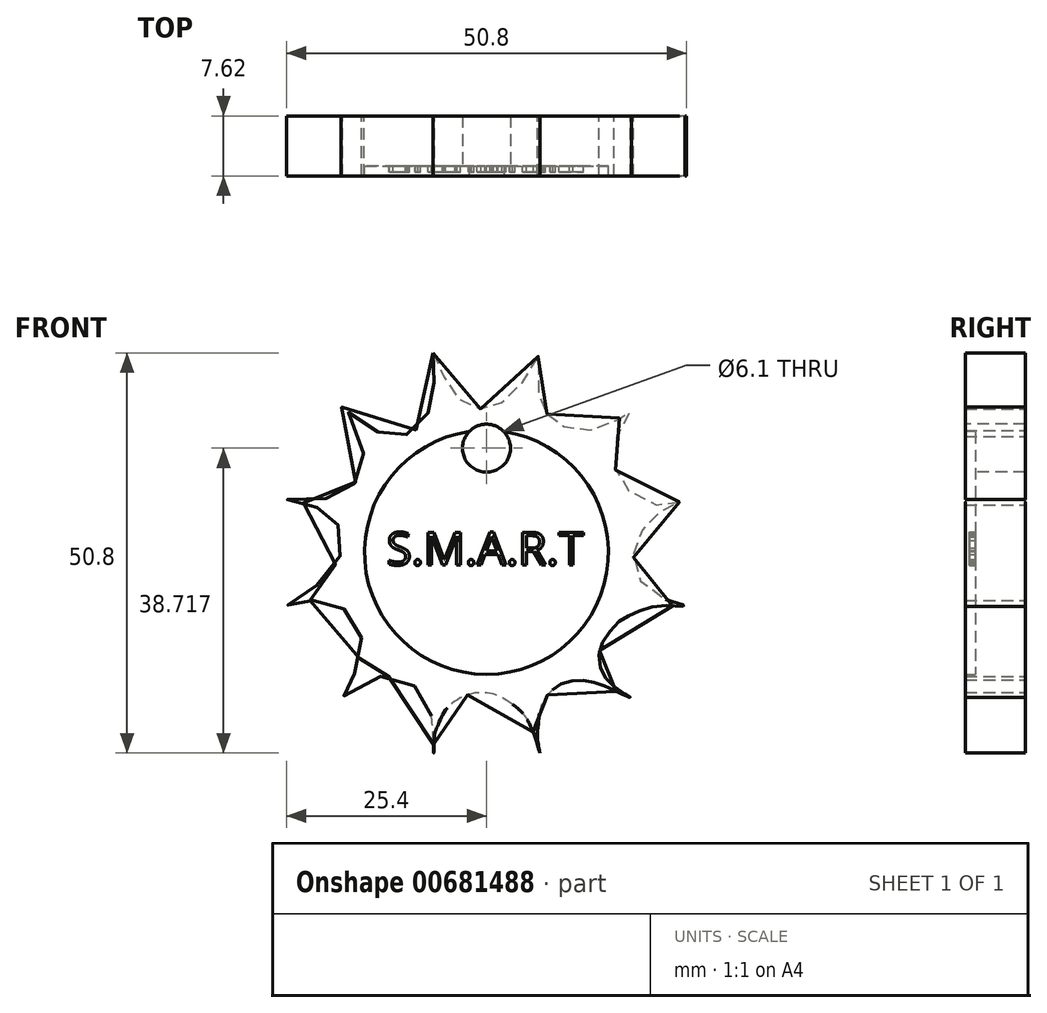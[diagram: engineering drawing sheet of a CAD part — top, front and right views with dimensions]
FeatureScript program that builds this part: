
annotation { "Feature Type Name" : "Feature", "Feature Type Description" : "" }
export const myFeature = defineFeature(function(context is Context, id is Id, definition is map)
    precondition{}
    {
        {
            var Q0;
            Q0=qCreatedBy(makeId("Front.planeOp"),FACE);
            var sketch = newSketch(context, id + "F0", { "sketchPlane" : qUnion([Q0])});
            skLineSegment(sketch, "E0", {"start": v(0, 25.32) * mm, "end": v(0, -36.27) * mm, "construction": true});
            skCircle(sketch, "E1", {"center": v(0, 0) * mm, "radius": 15.5 * mm});
            skFitSpline(sketch, "E2", {"points": [v(-6.8, 25.32) * mm, v(-6.05, 23.64) * mm, v(-5.33, 22.11) * mm, v(-4.49, 20.65) * mm, v(-3.23, 19.2) * mm, v(-1.8, 18.43) * mm, v(-0.62, 18.22) * mm, v(0.84, 18.43) * mm, v(1.9, 19) * mm, v(3.51, 20.38) * mm, v(4.9, 21.96) * mm, v(6.03, 23.61) * mm, v(6.78, 25.32) * mm, v(6.78, 24.57) * mm, v(6.57, 23.28) * mm, v(6.48, 21.66) * mm, v(6.6, 20.2) * mm, v(7.02, 18.73) * mm, v(7.56, 17.74) * mm, v(8.05, 17.24) * mm, v(9.13, 16.4) * mm, v(10.79, 15.65) * mm, v(12.62, 15.47) * mm, v(14.4, 15.78) * mm, v(16.6, 16.82) * mm, v(18.38, 18.46) * mm, v(18.38, 18.22) * mm, v(17.56, 16.96) * mm, v(16.64, 15.09) * mm, v(16.23, 12.47) * mm, v(16.39, 10.47) * mm, v(17.17, 8.9) * mm, v(18.5, 7.48) * mm, v(20.75, 6.23) * mm, v(24.01, 6.21) * mm, v(25.23, 6.75) * mm, v(23.23, 5.73) * mm, v(21.86, 4.98) * mm, v(20.45, 3.68) * mm, v(19.67, 2.68) * mm, v(18.91, 1.21) * mm, v(18.66, -0.73) * mm, v(19.1, -2.7) * mm, v(20.07, -4.33) * mm, v(22.27, -5.82) * mm, v(25.4, -6.82) * mm, v(23.2, -6.77) * mm, v(20.35, -7.13) * mm, v(18.3, -7.93) * mm, v(16.78, -8.82) * mm, v(15.22, -10.69) * mm, v(14.33, -12.8) * mm, v(14.66, -15.14) * mm, v(15.66, -16.51) * mm, v(17.33, -17.83) * mm, v(18.29, -18.42) * mm, v(17.5, -18.15) * mm, v(16.44, -17.66) * mm, v(15.3, -17.09) * mm, v(13.8, -16.54) * mm, v(12.12, -16.24) * mm, v(10.32, -16.43) * mm, v(8.88, -17.06) * mm, v(7.8, -18.06) * mm, v(6.95, -19.52) * mm, v(6.53, -22.35) * mm, v(6.48, -23.79) * mm, v(6.78, -25.48) * mm, v(6.31, -23.92) * mm, v(5.68, -22.28) * mm, v(4.72, -20.57) * mm, v(2.86, -19.02) * mm, v(1.27, -18.15) * mm, v(-0.45, -17.81) * mm, v(-2.2, -18.05) * mm, v(-3.86, -18.8) * mm, v(-5.3, -20.19) * mm, v(-6.19, -21.99) * mm, v(-6.61, -23.34) * mm, v(-6.7, -25.48) * mm, v(-6.78, -23.32) * mm, v(-6.9, -21.56) * mm, v(-7.33, -19.25) * mm, v(-8.8, -17.28) * mm, v(-10.64, -16.12) * mm, v(-13.35, -15.74) * mm, v(-16.42, -16.75) * mm, v(-18.44, -18.5) * mm, v(-17.52, -16.97) * mm, v(-16.38, -14.34) * mm, v(-15.87, -11.84) * mm, v(-16.23, -9.2) * mm, v(-17.76, -7.43) * mm, v(-19.9, -6.4) * mm, v(-21.63, -6.12) * mm, v(-24.18, -6.35) * mm, v(-25.4, -6.84) * mm, v(-23.88, -5.8) * mm, v(-21.95, -4.55) * mm, v(-20.23, -2.91) * mm, v(-18.52, -0.35) * mm, v(-18.31, 1.55) * mm, v(-18.87, 3.52) * mm, v(-19.87, 4.58) * mm, v(-21.05, 5.42) * mm, v(-23.12, 6.24) * mm, v(-25.4, 6.7) * mm, v(-23.1, 6.7) * mm, v(-20.26, 6.87) * mm, v(-18.1, 7.6) * mm, v(-16.57, 8.99) * mm, v(-15.68, 10.72) * mm, v(-15.7, 12.86) * mm, v(-16.45, 15.3) * mm, v(-17.3, 16.86) * mm, v(-18.5, 18.4) * mm, v(-18.4, 18.45) * mm, v(-16.72, 17) * mm, v(-14.82, 15.79) * mm, v(-12.58, 14.86) * mm, v(-11.3, 14.72) * mm, v(-9.6, 15.17) * mm, v(-8.25, 16.3) * mm, v(-7.19, 18.27) * mm, v(-6.81, 19.94) * mm, v(-6.65, 21.94) * mm, v(-6.65, 23.9) * mm, v(-6.8, 25.32) * mm]});
            skSolve(sketch);
        }
        {
            var Q0;
            Q0 = qSketchRegion(id + "F0", true);
            extrude(context, id + "F1", {"entities" : qUnion([Q0]), "depth" : 7.62 * mm, "offsetDistance" : 25.4 * mm});
        }
        {
            var Q0;
            Q0=qCreatedBy(makeId("Front.planeOp"),FACE);
            var sketch = newSketch(context, id + "F2", { "sketchPlane" : qUnion([Q0])});
            skCircle(sketch, "E3", {"center": v(0, 0) * mm, "radius": 16.85 * mm});
            skSolve(sketch);
        }
        {
            var Q0;
            Q0 = qSketchRegion(id + "F2", true);
            extrude(context, id + "F3", {"entities" : qUnion([Q0]), "operationType" : NewBodyOperationType.ADD, "depth" : 6.35 * mm, "offsetDistance" : 25.4 * mm});
        }
        {
            var Q0;
            Q0=makeQuery(id+"F3.opExtrude","CAP_FACE",FACE,{"disambiguationData":[OSD([sQuery(id+"F2.wireOp",EDGE,"E3")])],"isStart":false});
            var sketch = newSketch(context, id + "F4", { "sketchPlane" : qUnion([Q0])});
            skText(sketch, "E4", { "text": "S.M.A.R.T", "fontName": "OpenSans-Regular.ttf"});
            skLineSegment(sketch, "E5", {"start": v(0, 13.55) * mm, "end": v(0, -11.19) * mm, "construction": true});
            const initialGuessF4  = {"E4": [-0.0127, -0.0016, 1, 0, 0.00418]};
            skSetInitialGuess(sketch, initialGuessF4);
            skSolve(sketch);
        }
        {
            var Q0;
            Q0 = qSketchRegion(id + "F4", true);
            extrude(context, id + "F5", {"entities" : qUnion([Q0]), "operationType" : NewBodyOperationType.ADD, "depth" : 0.76 * mm, "offsetDistance" : 25.4 * mm});
        }
        {
            var Q0;
            Q0=qCreatedBy(makeId("Front.planeOp"),FACE);
            var sketch = newSketch(context, id + "F6", { "sketchPlane" : qUnion([Q0])});
            skCircle(sketch, "E6", {"center": v(0, 13.24) * mm, "radius": 3.05 * mm});
            skSolve(sketch);
        }
        {
            var Q0;
            Q0 = qSketchRegion(id + "F6", true);
            extrude(context, id + "F7", {"entities" : qUnion([Q0]), "operationType" : NewBodyOperationType.REMOVE, "endBound" : BoundingType.SYMMETRIC, "oppositeDirection" : true, "depth" : 152.4 * mm, "offsetDistance" : 25.4 * mm});
        }
    });
